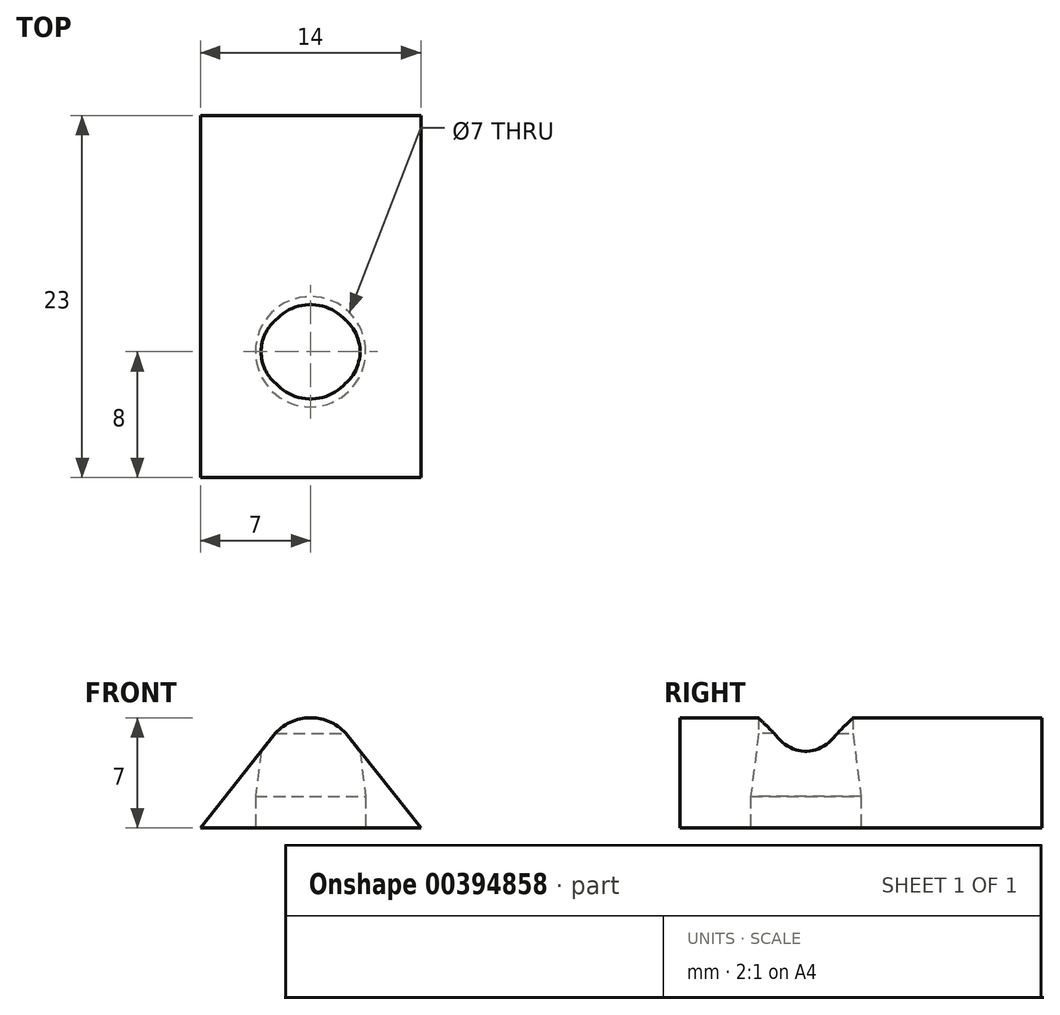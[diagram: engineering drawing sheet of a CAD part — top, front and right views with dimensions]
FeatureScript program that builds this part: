
annotation { "Feature Type Name" : "Feature", "Feature Type Description" : "" }
export const myFeature = defineFeature(function(context is Context, id is Id, definition is map)
    precondition{}
    {
        {
            var Q0;
            Q0=qCreatedBy(makeId("Front.planeOp"),FACE);
            var sketch = newSketch(context, id + "F0", { "sketchPlane" : qUnion([Q0])});
            skLineSegment(sketch, "E0", {"start": v(-7, 0) * mm, "end": v(7, 0) * mm});
            skLineSegment(sketch, "E1", {"start": v(-7, 0) * mm, "end": v(-2.35, 5.86) * mm});
            skLineSegment(sketch, "E2", {"start": v(2.35, 5.86) * mm, "end": v(7, 0) * mm});
            skPoint(sketch, "E3.visualSharp", {"position": v(0, 8.83) * mm});
            skArc(sketch, "E3.filletArc", {"start": v(2.35, 5.86) * mm, "mid": v(0, 7) * mm, "end": v(-2.35, 5.86) * mm});
            skSolve(sketch);
        }
        {
            var Q0;
            Q0 = qSketchRegion(id + "F0", true);
            extrude(context, id + "F1", {"entities" : qUnion([Q0]), "depth" : (4 + 4) * mm, "hasSecondDirection" : true, "secondDirectionOppositeDirection" : true, "secondDirectionDepth" : (23 - 8) * mm});
        }
        {
            var Q0;
            Q0=qCreatedBy(makeId("Front.planeOp"),FACE);
            var sketch = newSketch(context, id + "F2", { "sketchPlane" : qUnion([Q0])});
            skLineSegment(sketch, "E4", {"start": v(-3.5, 2) * mm, "end": v(-3.5, 0) * mm});
            skLineSegment(sketch, "E5", {"start": v(0, 6) * mm, "end": v(0, 0) * mm});
            skLineSegment(sketch, "E6", {"start": v(0, 0) * mm, "end": v(-3.5, 0) * mm});
            skLineSegment(sketch, "E7", {"start": v(-3.5, 2) * mm, "end": v(-3, 6) * mm});
            skLineSegment(sketch, "E8", {"start": v(0, 6) * mm, "end": v(-3, 6) * mm});
            skLineSegment(sketch, "E9", {"start": v(-3, 6) * mm, "end": v(-3, 8) * mm});
            skLineSegment(sketch, "E10", {"start": v(-3, 8) * mm, "end": v(0, 8) * mm});
            skLineSegment(sketch, "E11", {"start": v(0, 8) * mm, "end": v(0, 6) * mm});
            skLineSegment(sketch, "E12", {"start": v(0, 17.94) * mm, "end": v(0, -9.04) * mm, "construction": true});
            skSolve(sketch);
        }
        {
            var Q0;
            Q0 = qSketchRegion(id + "F2", true);
            var Q1;
            Q1=sQuery(id+"F2.wireOp",EDGE,"E12");
            revolve(context, id + "F3", {"operationType" : NewBodyOperationType.REMOVE, "entities" : qUnion([Q0]), "axis" : qUnion([Q1]), "revolveType" : RevolveType.FULL, "oppositeDirection" : true});
        }
    });
